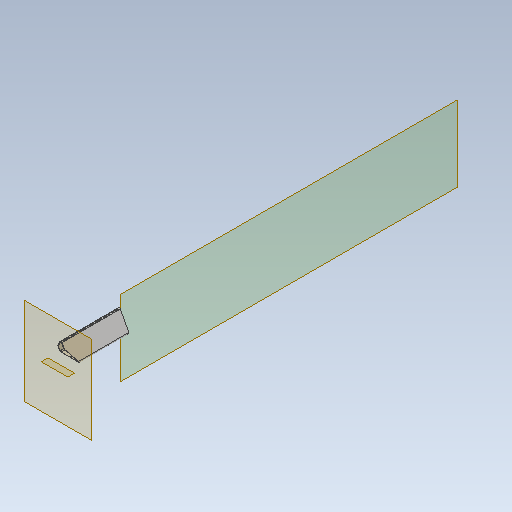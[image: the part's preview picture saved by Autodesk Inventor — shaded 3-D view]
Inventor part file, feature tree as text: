
AUTODESK INVENTOR PART (.ipt)
format: ipt  version: 2020.1 (Build 241239000, 239)  size: 457,216 bytes
history: native  units: mm
features: sheet_metal_op x8, other x7, plane x4, sketch x4, reference x3, extrude x1, projected_geometry x1
ambient origin geometry x8: Origin, YZ Plane, XZ Plane, XY Plane, X Axis, Y Axis, Z Axis, Center Point
bodies: Body1 (feature_tree)
feature tree (28):
  plane  "Work Plane1"
  plane  "Work Plane3"
  sheet_metal_op  "Contour Flange2"
  sheet_metal_op  "Flange1"
  plane  "Work Plane4"
  extrude  "Extrusion1"  Depth=10.0mm
  sheet_metal_op  "Unfold1"
  sheet_metal_op  "Refold1"
  sketch  "Sketch1"  dims[d12=10.0mm d13=10.0mm]
  reference  "Reference1"
  reference  "Reference2"
  reference  "Reference3"
  plane  "Work Plane2"
  other  "Plate2"
  sheet_metal_op  "Bend2"
  sheet_metal_op  "Corner2"
  sketch  "Sketch3"  dims[d14=2.0mm]
  other  "Plate3"
  sheet_metal_op  "Bend3"
  sheet_metal_op  "Corner3"
  sketch  "Sketch4"  dims[d15=2.0mm]
  sketch  "Sketch5"  dims[d16=1.0mm d17=4.0mm d18=2.0mm d19=200.0mm d20=2.0mm d21=2.0mm d22=8.0mm d23=2.0mm d24=2.0mm d25=2.0mm d26=1.0mm d27=4.0mm d28=2.0mm d29=33.477mm d30=20.628046mm d31=2.0mm d32=8.0mm d33=2.0mm d34=2.0mm d37=10.0mm d38=0.0mm d39=5.674267mm d40=2.837133mm d41=6.0mm d42=21.0mm d43=5.5mm d44=70.0mm d46=26.5mm d47=10.0mm d49=10.0mm d51=2.0mm d52=0.0mm d53=5.986479mm d54=10.0mm d55=5.5mm]
  projected_geometry  "Projected Loop1"
  other  "Cut1"
  parser-record x1  (decoder bookkeeping rows leaked as tree rows — omitted from the tree; the rows remain in map.json)
  other  "svejselære.iam"
  other  "plade:1"
  other  "Definition1"
note: 1 file-system path scrubbed to <path> (originals preserved in map.json)
